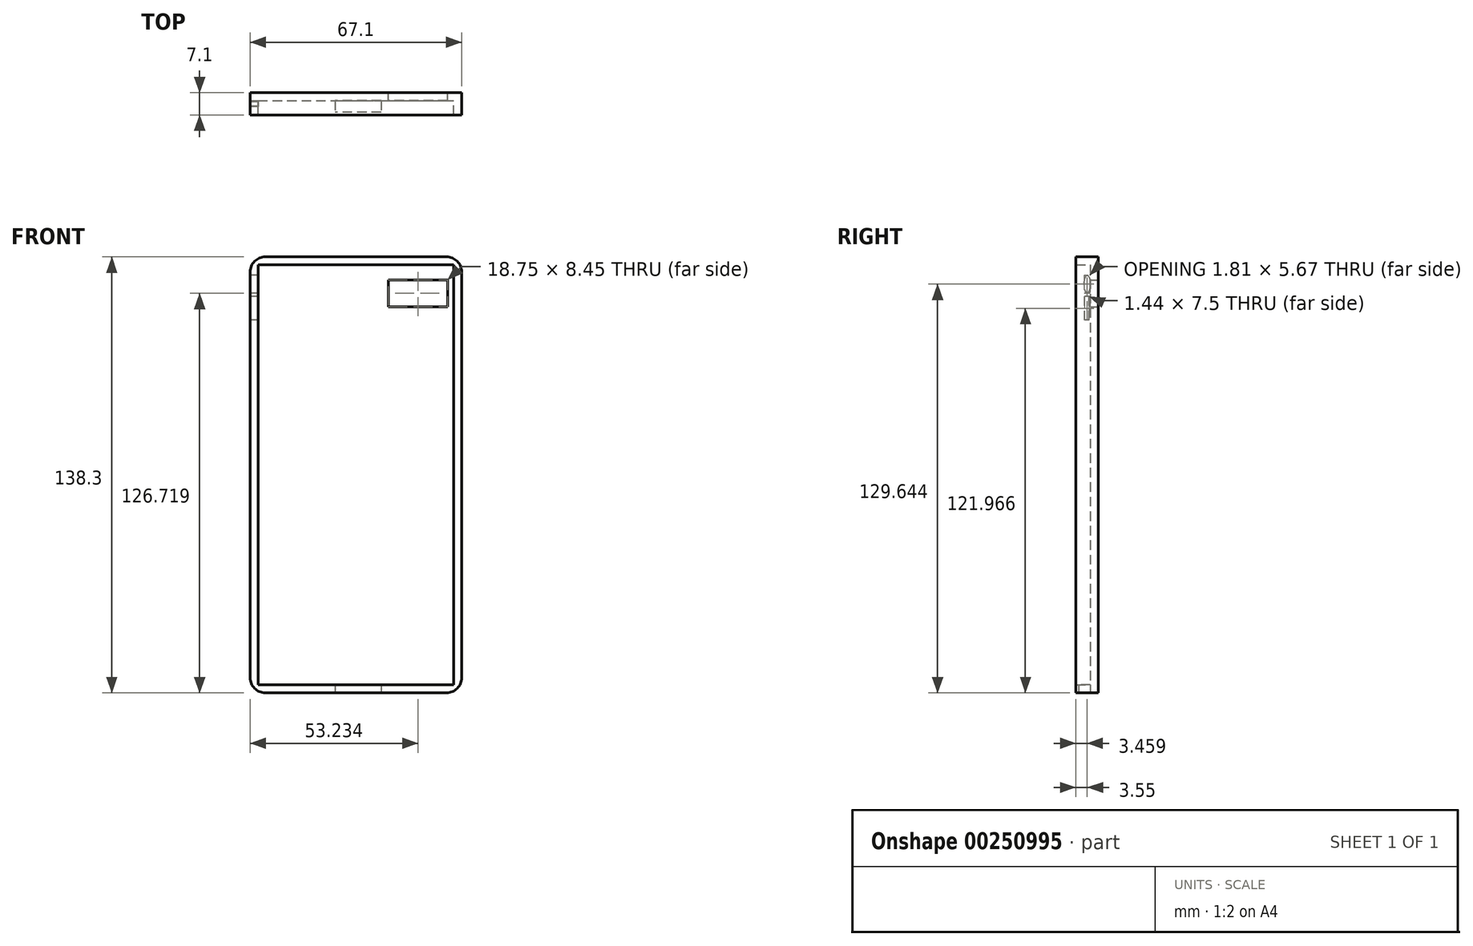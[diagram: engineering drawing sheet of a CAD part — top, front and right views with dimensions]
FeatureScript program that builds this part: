
annotation { "Feature Type Name" : "Feature", "Feature Type Description" : "" }
export const myFeature = defineFeature(function(context is Context, id is Id, definition is map)
    precondition{}
    {
        {
            var Q0;
            Q0=qCreatedBy(makeId("Front.planeOp"),FACE);
            var sketch = newSketch(context, id + "F0", { "sketchPlane" : qUnion([Q0])});
            skLineSegment(sketch, "E0.bottom", {"start": v(-55.44, 71.44) * mm, "end": v(11.66, 71.44) * mm});
            skLineSegment(sketch, "E0.top", {"start": v(-55.44, -66.86) * mm, "end": v(11.66, -66.86) * mm});
            skLineSegment(sketch, "E0.left", {"start": v(-55.44, 71.44) * mm, "end": v(-55.44, -66.86) * mm});
            skLineSegment(sketch, "E0.right", {"start": v(11.66, 71.44) * mm, "end": v(11.66, -66.86) * mm});
            skSolve(sketch);
        }
        {
            var Q0;
            Q0=makeQuery(id+"F0.imprint","IMPRINT",FACE,{"disambiguationData":[TD([[makeQuery(id+"F0.imprint","IMPRINT",EDGE,{"derivedFrom":sQuery(id+"F0.wireOp",EDGE,"E0.bottom")}),-1.0]])]});
            extrude(context, id + "F1", {"entities" : qUnion([Q0]), "endBound" : BoundingType.SYMMETRIC, "depth" : 7.1 * mm});
        }
        {
            var Q0;
            Q0=makeQuery(id+"F1.opExtrude","CAP_FACE",FACE,{"disambiguationData":[OSD([sQuery(id+"F0.wireOp",EDGE,"E0.bottom"),sQuery(id+"F0.wireOp",EDGE,"E0.top"),sQuery(id+"F0.wireOp",EDGE,"E0.left"),sQuery(id+"F0.wireOp",EDGE,"E0.right")])],"isStart":false});
            shell(context, id + "F2", {"entities" : qUnion([Q0]), "thickness" : 2.54 * mm});
        }
        {
            var Q0;
            Q0=makeQuery(id+"F1.opExtrude","SWEPT_EDGE",EDGE,{"disambiguationData":[OSD([sQuery(id+"F0.wireOp",EDGE,"E0.bottom"),sQuery(id+"F0.wireOp",EDGE,"E0.left")])]});
            var Q1;
            Q1=makeQuery(id+"F1.opExtrude","SWEPT_EDGE",EDGE,{"disambiguationData":[OSD([sQuery(id+"F0.wireOp",EDGE,"E0.bottom"),sQuery(id+"F0.wireOp",EDGE,"E0.right")])]});
            var Q2;
            Q2=makeQuery(id+"F1.opExtrude","SWEPT_EDGE",EDGE,{"disambiguationData":[OSD([sQuery(id+"F0.wireOp",EDGE,"E0.top"),sQuery(id+"F0.wireOp",EDGE,"E0.right")])]});
            var Q3;
            Q3=makeQuery(id+"F1.opExtrude","SWEPT_EDGE",EDGE,{"disambiguationData":[OSD([sQuery(id+"F0.wireOp",EDGE,"E0.top"),sQuery(id+"F0.wireOp",EDGE,"E0.left")])]});
            fillet(context, id + "F3", {"entities" : qUnion([Q0, Q1, Q2, Q3]), "radius" : 4.83 * mm, "tangentPropagation" : true, "allowEdgeOverflow" : false});
        }
        {
            var Q0;
            Q0=qCreatedBy(makeId("Front.planeOp"),FACE);
            var sketch = newSketch(context, id + "F4", { "sketchPlane" : qUnion([Q0])});
            skLineSegment(sketch, "E1.bottom", {"start": v(-11.58, 64.08) * mm, "end": v(7.17, 64.08) * mm});
            skLineSegment(sketch, "E1.top", {"start": v(-11.58, 55.63) * mm, "end": v(7.17, 55.63) * mm});
            skLineSegment(sketch, "E1.left", {"start": v(-11.58, 64.08) * mm, "end": v(-11.58, 55.63) * mm});
            skLineSegment(sketch, "E1.right", {"start": v(7.17, 64.08) * mm, "end": v(7.17, 55.63) * mm});
            skSolve(sketch);
        }
        {
            var Q0;
            Q0 = qSketchRegion(id + "F4", true);
            extrude(context, id + "F5", {"entities" : qUnion([Q0]), "operationType" : NewBodyOperationType.REMOVE, "endBound" : BoundingType.SYMMETRIC, "depth" : 25 * mm});
        }
        {
            var Q0;
            Q0=makeQuery(id+"F1.opExtrude","SWEPT_FACE",FACE,{"disambiguationData":[OSD([sQuery(id+"F0.wireOp",EDGE,"E0.top")])]});
            var sketch = newSketch(context, id + "F6", { "sketchPlane" : qUnion([Q0])});
            skLineSegment(sketch, "E2.bottom", {"start": v(-28.46, 2.7) * mm, "end": v(-13.9, 2.7) * mm});
            skLineSegment(sketch, "E2.top", {"start": v(-28.46, -1.02) * mm, "end": v(-13.9, -1.02) * mm});
            skLineSegment(sketch, "E2.left", {"start": v(-28.46, 2.7) * mm, "end": v(-28.46, -1.02) * mm});
            skLineSegment(sketch, "E2.right", {"start": v(-13.9, 2.7) * mm, "end": v(-13.9, -1.02) * mm});
            skSolve(sketch);
        }
        {
            var Q0;
            Q0 = qSketchRegion(id + "F6", true);
            extrude(context, id + "F7", {"entities" : qUnion([Q0]), "operationType" : NewBodyOperationType.REMOVE, "endBound" : BoundingType.SYMMETRIC, "oppositeDirection" : true, "depth" : 25 * mm});
        }
        {
            var Q0;
            Q0=makeQuery(id+"F1.opExtrude","SWEPT_FACE",FACE,{"disambiguationData":[OSD([sQuery(id+"F0.wireOp",EDGE,"E0.left")])]});
            var sketch = newSketch(context, id + "F8", { "sketchPlane" : qUnion([Q0])});
            skEllipse(sketch, "E3", {"center": v(0, 62.78) * mm, "majorRadius": 2.84 * mm, "minorRadius": 0.9 * mm, "majorAxis": v(0, 1)});
            skLineSegment(sketch, "E4.bottom", {"start": v(0.81, 58.86) * mm, "end": v(-0.63, 58.86) * mm});
            skLineSegment(sketch, "E4.top", {"start": v(0.81, 51.35) * mm, "end": v(-0.63, 51.35) * mm});
            skLineSegment(sketch, "E4.left", {"start": v(0.81, 58.86) * mm, "end": v(0.81, 51.35) * mm});
            skLineSegment(sketch, "E4.right", {"start": v(-0.63, 58.86) * mm, "end": v(-0.63, 51.35) * mm});
            skSolve(sketch);
        }
        {
            var Q0;
            Q0=makeQuery(id+"F8.imprint","IMPRINT",FACE,{"disambiguationData":[TD([[makeQuery(id+"F8.imprint","IMPRINT",EDGE,{"derivedFrom":sQuery(id+"F8.wireOp",EDGE,"E3")}),1.0]])]});
            var Q1;
            Q1=makeQuery(id+"F8.imprint","IMPRINT",FACE,{"disambiguationData":[TD([[makeQuery(id+"F8.imprint","IMPRINT",EDGE,{"derivedFrom":sQuery(id+"F8.wireOp",EDGE,"E4.bottom")}),1.0]])]});
            extrude(context, id + "F9", {"entities" : qUnion([Q0, Q1]), "operationType" : NewBodyOperationType.REMOVE, "endBound" : BoundingType.SYMMETRIC, "oppositeDirection" : true, "depth" : 25 * mm});
        }
    });
